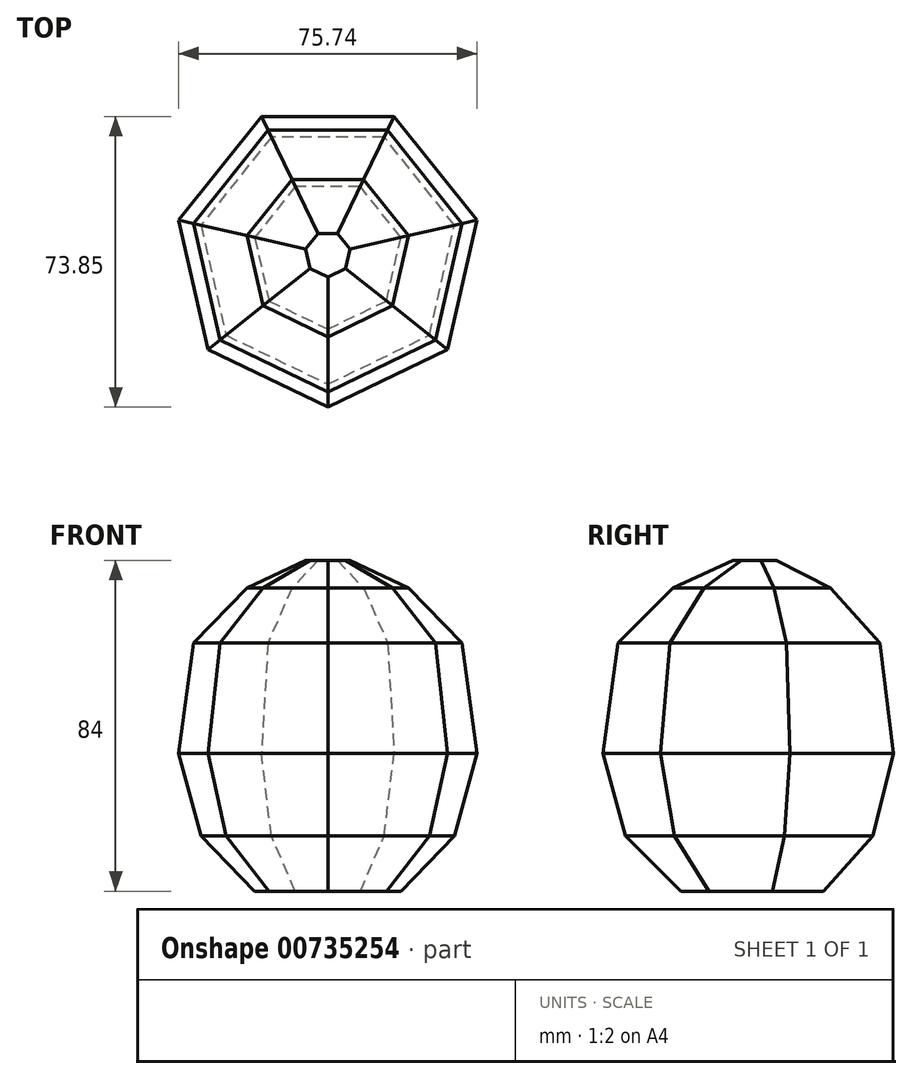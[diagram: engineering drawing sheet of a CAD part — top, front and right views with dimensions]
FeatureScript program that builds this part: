
annotation { "Feature Type Name" : "Feature", "Feature Type Description" : "" }
export const myFeature = defineFeature(function(context is Context, id is Id, definition is map)
    precondition{}
    {
        {
            var Q0;
            Q0=qCreatedBy(makeId("Top.planeOp"),FACE);
            var sketch = newSketch(context, id + "F0", { "sketchPlane" : qUnion([Q0])});
            skCircle(sketch, "E0.cCircle", {"center": v(0, 0) * mm, "radius": 35 * mm, "construction": true});
            skLineSegment(sketch, "E0.0", {"start": v(-16.86, 35) * mm, "end": v(16.86, 35) * mm});
            skLineSegment(sketch, "E0.1", {"start": v(16.86, 35) * mm, "end": v(37.87, 8.64) * mm});
            skLineSegment(sketch, "E0.2", {"start": v(37.87, 8.64) * mm, "end": v(30.37, -24.22) * mm});
            skLineSegment(sketch, "E0.3", {"start": v(30.37, -24.22) * mm, "end": v(0, -38.85) * mm});
            skLineSegment(sketch, "E0.4", {"start": v(0, -38.85) * mm, "end": v(-30.37, -24.22) * mm});
            skLineSegment(sketch, "E0.5", {"start": v(-30.37, -24.22) * mm, "end": v(-37.87, 8.64) * mm});
            skLineSegment(sketch, "E0.6", {"start": v(-37.87, 8.64) * mm, "end": v(-16.86, 35) * mm});
            skPoint(sketch, "E0.0.midPoint", {"position": v(0, 35) * mm});
            skSolve(sketch);
        }
        {
            var Q0;
            Q0=makeQuery(id+"F0.imprint","IMPRINT",FACE,{"disambiguationData":[TD([[makeQuery(id+"F0.imprint","IMPRINT",EDGE,{"derivedFrom":sQuery(id+"F0.wireOp",EDGE,"E0.0")}),-1.0]])]});
            extrude(context, id + "F1", {"entities" : qUnion([Q0]), "depth" : 28 * mm, "offsetDistance" : 25 * mm, "hasDraft" : true, "draftAngle" : 7 * degree, "draftPullDirection" : true});
        }
        {
            var Q0;
            Q0=makeQuery(id+"F1.opExtrude","CAP_FACE",FACE,{"disambiguationData":[OSD([sQuery(id+"F0.wireOp",EDGE,"E0.0"),sQuery(id+"F0.wireOp",EDGE,"E0.1"),sQuery(id+"F0.wireOp",EDGE,"E0.2"),sQuery(id+"F0.wireOp",EDGE,"E0.3"),sQuery(id+"F0.wireOp",EDGE,"E0.4"),sQuery(id+"F0.wireOp",EDGE,"E0.5"),sQuery(id+"F0.wireOp",EDGE,"E0.6")])],"isStart":false});
            extrude(context, id + "F2", {"entities" : qUnion([Q0]), "operationType" : NewBodyOperationType.ADD, "depth" : 14 * mm, "offsetDistance" : 25 * mm, "hasDraft" : true, "draftAngle" : 42 * degree, "draftPullDirection" : true});
        }
        {
            var Q0;
            Q0=makeQuery(id+"F2.opExtrude","CAP_FACE",FACE,{"disambiguationData":[OSD([sQuery(id+"F0.wireOp",EDGE,"E0.0"),sQuery(id+"F0.wireOp",EDGE,"E0.1"),sQuery(id+"F0.wireOp",EDGE,"E0.2"),sQuery(id+"F0.wireOp",EDGE,"E0.3"),sQuery(id+"F0.wireOp",EDGE,"E0.4"),sQuery(id+"F0.wireOp",EDGE,"E0.5"),sQuery(id+"F0.wireOp",EDGE,"E0.6")])],"isStart":false});
            extrude(context, id + "F3", {"entities" : qUnion([Q0]), "operationType" : NewBodyOperationType.ADD, "depth" : 7 * mm, "offsetDistance" : 25 * mm, "hasDraft" : true, "draftAngle" : 63 * degree, "draftPullDirection" : true});
        }
        {
            var Q0;
            Q0 = qSketchRegion(id + "F0", true);
            extrude(context, id + "F4", {"entities" : qUnion([Q0]), "operationType" : NewBodyOperationType.ADD, "oppositeDirection" : true, "depth" : 21 * mm, "offsetDistance" : 25 * mm, "hasDraft" : true, "draftAngle" : 14 * degree, "draftPullDirection" : true});
        }
        {
            var Q0;
            Q0=makeQuery(id+"F4.opExtrude","CAP_FACE",FACE,{"disambiguationData":[OSD([sQuery(id+"F0.wireOp",EDGE,"E0.0"),sQuery(id+"F0.wireOp",EDGE,"E0.1"),sQuery(id+"F0.wireOp",EDGE,"E0.2"),sQuery(id+"F0.wireOp",EDGE,"E0.3"),sQuery(id+"F0.wireOp",EDGE,"E0.4"),sQuery(id+"F0.wireOp",EDGE,"E0.5"),sQuery(id+"F0.wireOp",EDGE,"E0.6")])],"isStart":false});
            extrude(context, id + "F5", {"entities" : qUnion([Q0]), "operationType" : NewBodyOperationType.ADD, "depth" : 14 * mm, "offsetDistance" : 25 * mm, "hasDraft" : true, "draftAngle" : 42 * degree, "draftPullDirection" : true});
        }
    });
